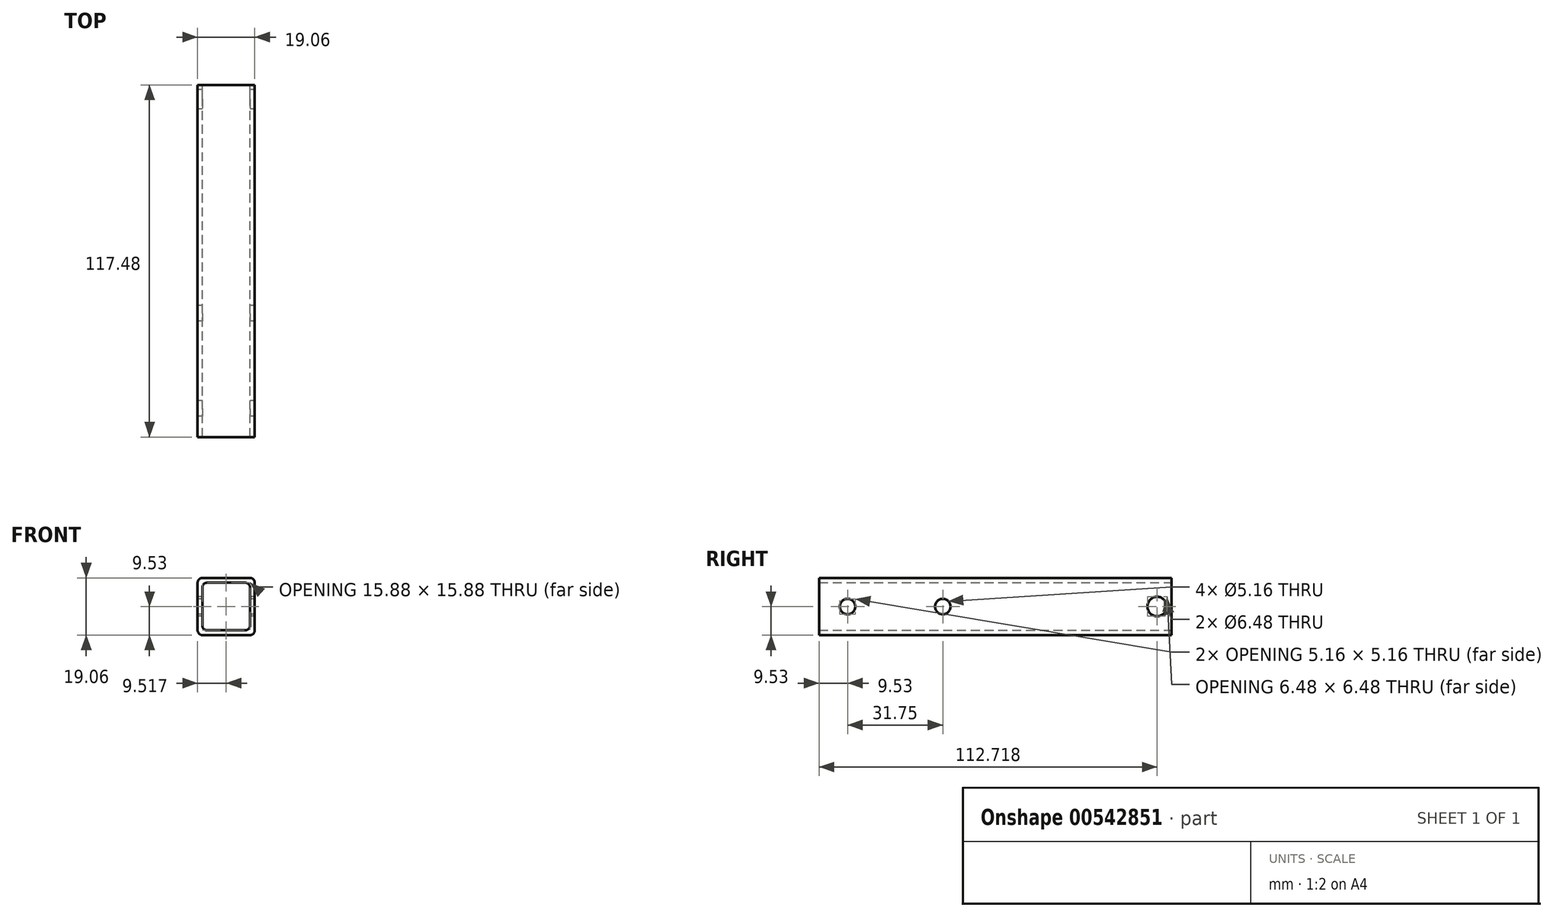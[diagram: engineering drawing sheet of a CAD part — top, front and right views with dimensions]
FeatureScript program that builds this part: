
annotation { "Feature Type Name" : "Feature", "Feature Type Description" : "" }
export const myFeature = defineFeature(function(context is Context, id is Id, definition is map)
    precondition{}
    {
        {
            var Q0;
            Q0=qCreatedBy(makeId("Front.planeOp"),FACE);
            var sketch = newSketch(context, id + "F0", { "sketchPlane" : qUnion([Q0])});
            skLineSegment(sketch, "E0.bottom", {"start": v(-9.53, 9.53) * mm, "end": v(9.53, 9.53) * mm});
            skLineSegment(sketch, "E0.top", {"start": v(-9.53, -9.53) * mm, "end": v(9.53, -9.53) * mm});
            skLineSegment(sketch, "E0.left", {"start": v(-9.53, 9.53) * mm, "end": v(-9.53, -9.53) * mm});
            skLineSegment(sketch, "E0.right", {"start": v(9.53, 9.53) * mm, "end": v(9.53, -9.53) * mm});
            skPoint(sketch, "E1", {"position": v(-9.53, 0) * mm});
            skPoint(sketch, "E2", {"position": v(9.53, 0) * mm});
            skPoint(sketch, "E3", {"position": v(0, -9.53) * mm});
            skPoint(sketch, "E4", {"position": v(0, 9.53) * mm});
            skLineSegment(sketch, "E5.bottom", {"start": v(-7.95, 7.94) * mm, "end": v(7.92, 7.94) * mm});
            skLineSegment(sketch, "E5.top", {"start": v(-7.95, -7.94) * mm, "end": v(7.92, -7.94) * mm});
            skLineSegment(sketch, "E5.left", {"start": v(-7.95, 7.94) * mm, "end": v(-7.95, -7.94) * mm});
            skLineSegment(sketch, "E5.right", {"start": v(7.92, 7.94) * mm, "end": v(7.92, -7.94) * mm});
            skSolve(sketch);
        }
        {
            var Q0;
            Q0=qSketchRegion(id+"F0",true);
            extrude(context, id + "F1", {"entities" : qUnion([Q0]), "depth" : 215.9 * mm, "offsetDistance" : 25.4 * mm, "symmetric" : true});
        }
        {
            var Q0;
            Q0=makeQuery(id+"F1.opExtrude","SWEPT_EDGE",EDGE,{"disambiguationData":[OSD([sQuery(id+"F0.wireOp",EDGE,"E0.bottom"),sQuery(id+"F0.wireOp",EDGE,"E0.left")])]});
            var Q1;
            Q1=makeQuery(id+"F1.opExtrude","SWEPT_EDGE",EDGE,{"disambiguationData":[OSD([sQuery(id+"F0.wireOp",EDGE,"E0.top"),sQuery(id+"F0.wireOp",EDGE,"E0.left")])]});
            var Q2;
            Q2=makeQuery(id+"F1.opExtrude","SWEPT_EDGE",EDGE,{"disambiguationData":[OSD([sQuery(id+"F0.wireOp",EDGE,"E0.top"),sQuery(id+"F0.wireOp",EDGE,"E0.right")])]});
            var Q3;
            Q3=makeQuery(id+"F1.opExtrude","SWEPT_EDGE",EDGE,{"disambiguationData":[OSD([sQuery(id+"F0.wireOp",EDGE,"E0.bottom"),sQuery(id+"F0.wireOp",EDGE,"E0.right")])]});
            fillet(context, id + "F2", {"entities" : qUnion([Q0, Q1, Q2, Q3]), "radius" : 1.59 * mm, "tangentPropagation" : true, "allowEdgeOverflow" : false});
        }
        {
            var Q0;
            Q0=makeQuery(id+"F1.opExtrude","SWEPT_EDGE",EDGE,{"disambiguationData":[OSD([sQuery(id+"F0.wireOp",EDGE,"E5.bottom"),sQuery(id+"F0.wireOp",EDGE,"E5.left")])]});
            var Q1;
            Q1=makeQuery(id+"F1.opExtrude","SWEPT_EDGE",EDGE,{"disambiguationData":[OSD([sQuery(id+"F0.wireOp",EDGE,"E5.top"),sQuery(id+"F0.wireOp",EDGE,"E5.left")])]});
            var Q2;
            Q2=makeQuery(id+"F1.opExtrude","SWEPT_EDGE",EDGE,{"disambiguationData":[OSD([sQuery(id+"F0.wireOp",EDGE,"E5.bottom"),sQuery(id+"F0.wireOp",EDGE,"E5.right")])]});
            var Q3;
            Q3=makeQuery(id+"F1.opExtrude","SWEPT_EDGE",EDGE,{"disambiguationData":[OSD([sQuery(id+"F0.wireOp",EDGE,"E5.top"),sQuery(id+"F0.wireOp",EDGE,"E5.right")])]});
            fillet(context, id + "F3", {"entities" : qUnion([Q0, Q1, Q2, Q3]), "radius" : 1.59 * mm, "tangentPropagation" : true, "allowEdgeOverflow" : false});
        }
        {
            var Q0;
            Q0=makeQuery(id+"F1.opExtrude","SWEPT_FACE",FACE,{"disambiguationData":[OSD([sQuery(id+"F0.wireOp",EDGE,"E0.left")])]});
            var sketch = newSketch(context, id + "F4", { "sketchPlane" : qUnion([Q0])});
            skCircle(sketch, "E6", {"center": v(-103.19, 0) * mm, "radius": 3.24 * mm});
            skCircle(sketch, "E7", {"center": v(-31.75, 0) * mm, "radius": 2.58 * mm});
            skPoint(sketch, "E7.centerSnap0", {"position": v(-107.95, 0) * mm});
            skCircle(sketch, "E8", {"center": v(0, 0) * mm, "radius": 2.58 * mm});
            skSolve(sketch);
        }
        {
            var Q0;
            Q0=makeQuery(id+"F4.imprint","IMPRINT",FACE,{"disambiguationData":[TD([[makeQuery(id+"F4.imprint","IMPRINT",EDGE,{"derivedFrom":sQuery(id+"F4.wireOp",EDGE,"E6")}),1.0]])]});
            var Q1;
            Q1=makeQuery(id+"F4.imprint","IMPRINT",FACE,{"disambiguationData":[TD([[makeQuery(id+"F4.imprint","IMPRINT",EDGE,{"derivedFrom":sQuery(id+"F4.wireOp",EDGE,"E7")}),1.0]])]});
            var Q2;
            Q2=makeQuery(id+"F4.imprint","IMPRINT",FACE,{"disambiguationData":[TD([[makeQuery(id+"F4.imprint","IMPRINT",EDGE,{"derivedFrom":sQuery(id+"F4.wireOp",EDGE,"E8")}),1.0]])]});
            var Q3;
            Q3=sQuery(id+"F4.wireOp",EDGE,"E6");
            var Q4;
            Q4=sQuery(id+"F4.wireOp",EDGE,"E7");
            var Q5;
            Q5=sQuery(id+"F4.wireOp",EDGE,"E8");
            extrude(context, id + "F5", {"entities" : qUnion([Q0, Q1, Q2]), "operationType" : NewBodyOperationType.REMOVE, "surfaceEntities" : qUnion([Q3, Q4, Q5]), "oppositeDirection" : true, "depth" : 19.05 * mm, "offsetDistance" : 25.4 * mm});
        }
        {
            var Q0;
            Q0=makeQuery(id+"F1.opExtrude","CAP_FACE",FACE,{"disambiguationData":[OSD([sQuery(id+"F0.wireOp",EDGE,"E0.bottom"),sQuery(id+"F0.wireOp",EDGE,"E0.top"),sQuery(id+"F0.wireOp",EDGE,"E0.left"),sQuery(id+"F0.wireOp",EDGE,"E0.right"),sQuery(id+"F0.wireOp",EDGE,"E5.bottom"),sQuery(id+"F0.wireOp",EDGE,"E5.top"),sQuery(id+"F0.wireOp",EDGE,"E5.left"),sQuery(id+"F0.wireOp",EDGE,"E5.right")])],"isStart":false});
            extrude(context, id + "F6", {"entities" : qUnion([Q0]), "operationType" : NewBodyOperationType.REMOVE, "oppositeDirection" : true, "depth" : 98.42 * mm, "offsetDistance" : 25.4 * mm});
        }
    });
